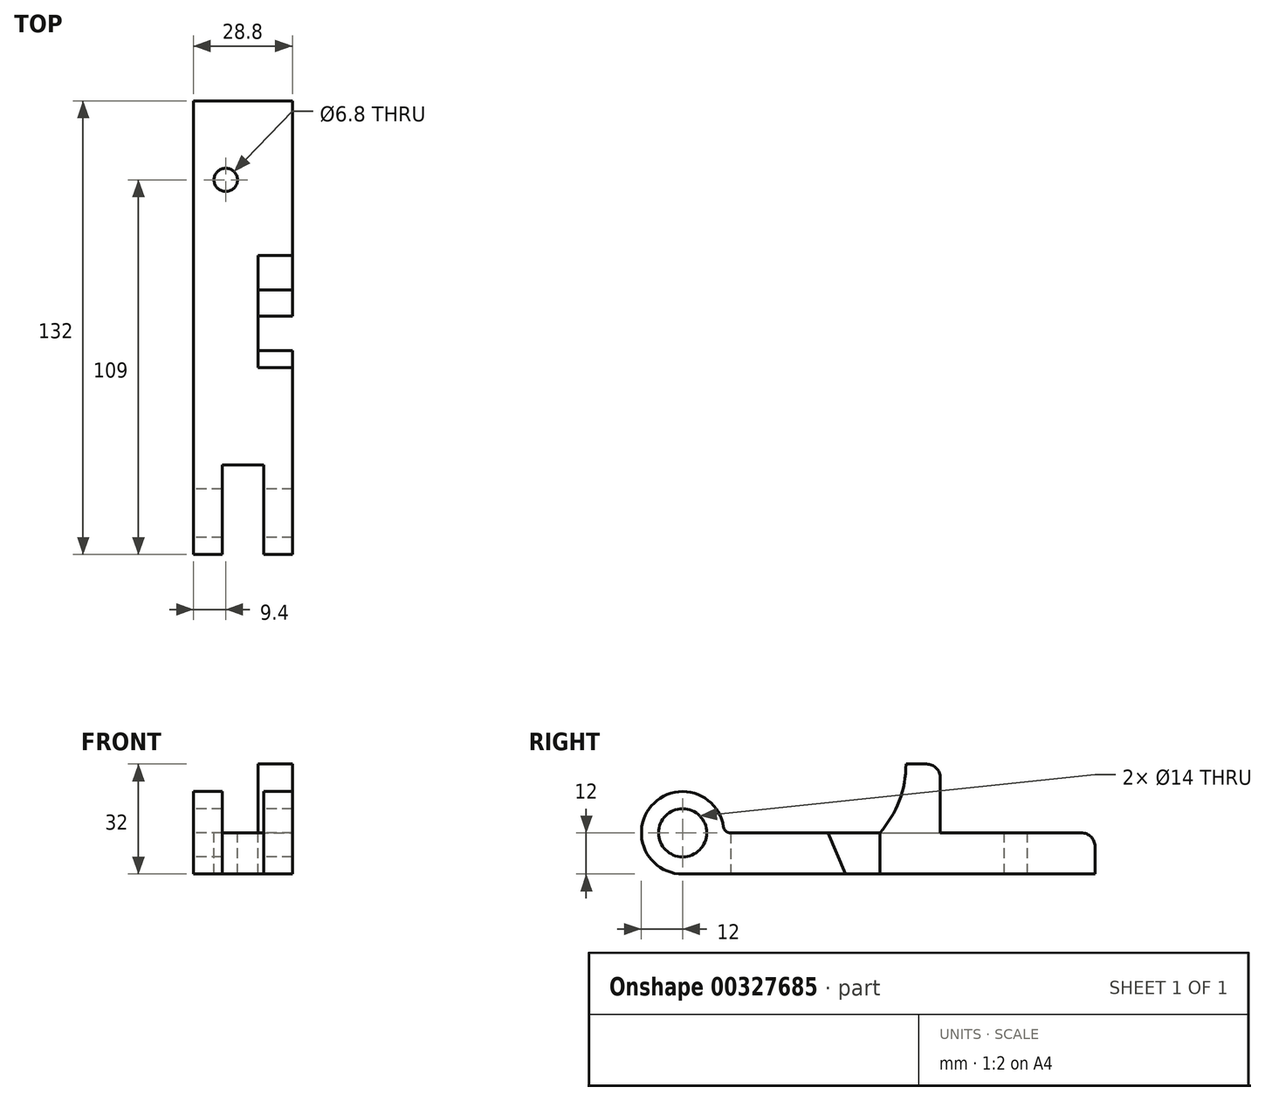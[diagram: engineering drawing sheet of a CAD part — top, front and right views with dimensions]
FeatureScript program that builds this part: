
annotation { "Feature Type Name" : "Feature", "Feature Type Description" : "" }
export const myFeature = defineFeature(function(context is Context, id is Id, definition is map)
    precondition{}
    {
        {
            var Q0;
            Q0=qCreatedBy(makeId("Right.planeOp"),FACE);
            var sketch = newSketch(context, id + "F0", { "sketchPlane" : qUnion([Q0])});
            skCircle(sketch, "E0", {"center": v(0, 0) * mm, "radius": 7 * mm});
            skArc(sketch, "E1", {"start": v(12, 0) * mm, "mid": v(-8.49, 8.49) * mm, "end": v(0, -12) * mm});
            skLineSegment(sketch, "E2.bottom", {"start": v(12, 0) * mm, "end": v(120, 0) * mm});
            skLineSegment(sketch, "E2.top", {"start": v(0, -12) * mm, "end": v(120, -12) * mm});
            skLineSegment(sketch, "E2.right", {"start": v(120, 0) * mm, "end": v(120, -12) * mm});
            skSolve(sketch);
        }
        {
            var Q0;
            Q0 = qSketchRegion(id + "F0", true);
            extrude(context, id + "F1", {"entities" : qUnion([Q0]), "depth" : 28.8 * mm});
        }
        {
            var Q0;
            Q0=makeQuery(id+"F1.opExtrude","CAP_FACE",FACE,{"disambiguationData":[OSD([sQuery(id+"F0.wireOp",EDGE,"E0"),sQuery(id+"F0.wireOp",EDGE,"E1"),sQuery(id+"F0.wireOp",EDGE,"E2.bottom"),sQuery(id+"F0.wireOp",EDGE,"E2.top"),sQuery(id+"F0.wireOp",EDGE,"E2.right")])],"isStart":false});
            cPlane(context, id + "F2", {"entities" : qUnion([Q0]), "cplaneType" : CPlaneType.OFFSET, "offset" : 8.4 * mm, "oppositeDirection" : true, "width" : 150 * mm, "height" : 150 * mm});
        }
        {
            var Q0;
            Q0=qCreatedBy(id+"F2.planeOp",FACE);
            var sketch = newSketch(context, id + "F3", { "sketchPlane" : qUnion([Q0])});
            skLineSegment(sketch, "E3", {"start": v(14, 0) * mm, "end": v(14, -12.12) * mm});
            skArc(sketch, "E4.0", {"start": v(12, 0) * mm, "mid": v(-8.49, 8.49) * mm, "end": v(0, -12) * mm});
            skLineSegment(sketch, "E5.0", {"start": v(0, -12) * mm, "end": v(14, -12) * mm});
            skPoint(sketch, "E6.orphan", {"position": v(120, -12) * mm});
            skLineSegment(sketch, "E7", {"start": v(12, 0) * mm, "end": v(14, 0) * mm});
            skSolve(sketch);
        }
        {
            var Q0;
            Q0 = qSketchRegion(id + "F3", true);
            extrude(context, id + "F4", {"entities" : qUnion([Q0]), "operationType" : NewBodyOperationType.REMOVE, "oppositeDirection" : true, "depth" : 12 * mm});
        }
        {
            var Q0;
            Q0=makeQuery(id+"F1.opExtrude","CAP_FACE",FACE,{"disambiguationData":[OSD([sQuery(id+"F0.wireOp",EDGE,"E0"),sQuery(id+"F0.wireOp",EDGE,"E1"),sQuery(id+"F0.wireOp",EDGE,"E2.bottom"),sQuery(id+"F0.wireOp",EDGE,"E2.top"),sQuery(id+"F0.wireOp",EDGE,"E2.right")])],"isStart":false});
            var sketch = newSketch(context, id + "F5", { "sketchPlane" : qUnion([Q0])});
            skLineSegment(sketch, "E8.bottom", {"start": v(75, 0) * mm, "end": v(65, 0) * mm});
            skLineSegment(sketch, "E8.top", {"start": v(75, 20) * mm, "end": v(65, 20) * mm});
            skLineSegment(sketch, "E8.left", {"start": v(75, 0) * mm, "end": v(75, 20) * mm});
            skLineSegment(sketch, "E8.right", {"start": v(65, 0) * mm, "end": v(65, 20) * mm, "construction": true});
            skArc(sketch, "E9", {"start": v(57.36, 0) * mm, "mid": v(63.02, 9.3) * mm, "end": v(65, 20) * mm});
            skLineSegment(sketch, "E10", {"start": v(57.36, 0) * mm, "end": v(65, 0) * mm});
            skSolve(sketch);
        }
        {
            var Q0;
            Q0 = qSketchRegion(id + "F5", true);
            extrude(context, id + "F6", {"entities" : qUnion([Q0]), "operationType" : NewBodyOperationType.ADD, "oppositeDirection" : true, "depth" : 10 * mm});
        }
        {
            var Q0;
            Q0=makeQuery(id+"F6.boolean.opBoolean","MERGE",FACE,{"derivedFrom":[makeQuery(id+"F1.opExtrude","CAP_FACE",FACE,{"disambiguationData":[OSD([sQuery(id+"F0.wireOp",EDGE,"E0"),sQuery(id+"F0.wireOp",EDGE,"E1"),sQuery(id+"F0.wireOp",EDGE,"E2.bottom"),sQuery(id+"F0.wireOp",EDGE,"E2.top"),sQuery(id+"F0.wireOp",EDGE,"E2.right")])],"isStart":false}),makeQuery(id+"F6.opExtrude","CAP_FACE",FACE,{"disambiguationData":[OSD([sQuery(id+"F5.wireOp",EDGE,"E8.bottom"),sQuery(id+"F5.wireOp",EDGE,"E8.top"),sQuery(id+"F5.wireOp",EDGE,"E8.left"),sQuery(id+"F5.wireOp",EDGE,"E9"),sQuery(id+"F5.wireOp",EDGE,"E10")])],"isStart":true})]});
            var sketch = newSketch(context, id + "F7", { "sketchPlane" : qUnion([Q0])});
            skLineSegment(sketch, "E11", {"start": v(57.36, 0) * mm, "end": v(57.36, -12) * mm});
            skLineSegment(sketch, "E12", {"start": v(57.36, -12) * mm, "end": v(47.36, -12) * mm});
            skLineSegment(sketch, "E13", {"start": v(47.36, -12) * mm, "end": v(42.36, 0) * mm});
            skLineSegment(sketch, "E14", {"start": v(42.36, 0) * mm, "end": v(57.36, 0) * mm});
            skSolve(sketch);
        }
        {
            var Q0;
            Q0 = qSketchRegion(id + "F7", true);
            var Q1;
            Q1=makeQuery(id+"F6.opExtrude","CAP_FACE",FACE,{"disambiguationData":[OSD([sQuery(id+"F5.wireOp",EDGE,"E8.bottom"),sQuery(id+"F5.wireOp",EDGE,"E8.top"),sQuery(id+"F5.wireOp",EDGE,"E8.left"),sQuery(id+"F5.wireOp",EDGE,"E9"),sQuery(id+"F5.wireOp",EDGE,"E10")])],"isStart":false});
            extrude(context, id + "F8", {"entities" : qUnion([Q0]), "operationType" : NewBodyOperationType.REMOVE, "endBound" : BoundingType.UP_TO_SURFACE, "oppositeDirection" : true, "endBoundEntityFace" : qUnion([Q1]), "depth" : 25 * mm});
        }
        {
            var Q0;
            Q0=qCreatedBy(makeId("Top.planeOp"),FACE);
            var sketch = newSketch(context, id + "F9", { "sketchPlane" : qUnion([Q0])});
            skLineSegment(sketch, "E15", {"start": v(0, 75) * mm, "end": v(18.8, 75) * mm, "construction": true});
            skPoint(sketch, "E16", {"position": v(9.4, 75) * mm});
            skCircle(sketch, "E17", {"center": v(9.4, 97) * mm, "radius": 3.4 * mm});
            skSolve(sketch);
        }
        {
            var Q0;
            Q0 = qSketchRegion(id + "F9", true);
            var Q1;
            Q1=makeQuery(id+"F1.opExtrude","SWEPT_FACE",FACE,{"disambiguationData":[OSD([sQuery(id+"F0.wireOp",EDGE,"E2.top")])]});
            extrude(context, id + "F10", {"entities" : qUnion([Q0]), "operationType" : NewBodyOperationType.REMOVE, "endBound" : BoundingType.UP_TO_SURFACE, "oppositeDirection" : true, "endBoundEntityFace" : qUnion([Q1]), "depth" : 25 * mm});
        }
        {
            var Q0;
            Q0=makeQuery(id+"F6.opExtrude","SWEPT_EDGE",EDGE,{"disambiguationData":[OSD([sQuery(id+"F0.wireOp",EDGE,"E2.bottom"),sQuery(id+"F5.wireOp",EDGE,"E8.bottom"),sQuery(id+"F5.wireOp",EDGE,"E8.left")])]});
            var Q1;
            {var subQ0=sQuery(id+"F0.wireOp",EDGE,"E2.bottom");var subQ1=sQuery(id+"F0.wireOp",EDGE,"E1");Q1=makeQuery(id+"F4.boolean.opBoolean","SPLIT",EDGE,{"disambiguationData":[TD([makeQuery(id+"F4.opExtrude","CAP_FACE",FACE,{"disambiguationData":[OSD([sQuery(id+"F3.wireOp",EDGE,"E3"),sQuery(id+"F3.wireOp",EDGE,"E4.0"),sQuery(id+"F3.wireOp",EDGE,"E5.0"),sQuery(id+"F3.wireOp",EDGE,"E7")])],"isStart":true})])],"derivedFrom":makeQuery(id+"F1.opExtrude","SWEPT_EDGE",EDGE,{"disambiguationData":[OSD([subQ1,subQ0])]})});}
            var Q2;
            {var subQ0=sQuery(id+"F0.wireOp",EDGE,"E2.bottom");var subQ1=sQuery(id+"F0.wireOp",EDGE,"E1");Q2=makeQuery(id+"F4.boolean.opBoolean","SPLIT",EDGE,{"disambiguationData":[TD([makeQuery(id+"F4.opExtrude","CAP_FACE",FACE,{"disambiguationData":[OSD([sQuery(id+"F3.wireOp",EDGE,"E3"),sQuery(id+"F3.wireOp",EDGE,"E4.0"),sQuery(id+"F3.wireOp",EDGE,"E5.0"),sQuery(id+"F3.wireOp",EDGE,"E7")])],"isStart":false})])],"derivedFrom":makeQuery(id+"F1.opExtrude","SWEPT_EDGE",EDGE,{"disambiguationData":[OSD([subQ1,subQ0])]})});}
            fillet(context, id + "F11", {"entities" : qUnion([Q0, Q1, Q2]), "radius" : 2 * mm, "tangentPropagation" : true, "allowEdgeOverflow" : false});
        }
        {
            var Q0;
            Q0=makeQuery(id+"F6.opExtrude","SWEPT_EDGE",EDGE,{"disambiguationData":[OSD([sQuery(id+"F5.wireOp",EDGE,"E8.top"),sQuery(id+"F5.wireOp",EDGE,"E8.left")])]});
            var Q1;
            Q1=makeQuery(id+"F1.opExtrude","SWEPT_EDGE",EDGE,{"disambiguationData":[OSD([sQuery(id+"F0.wireOp",EDGE,"E2.bottom"),sQuery(id+"F0.wireOp",EDGE,"E2.right")])]});
            fillet(context, id + "F12", {"entities" : qUnion([Q0, Q1]), "radius" : 4 * mm, "tangentPropagation" : true, "allowEdgeOverflow" : false});
        }
    });
